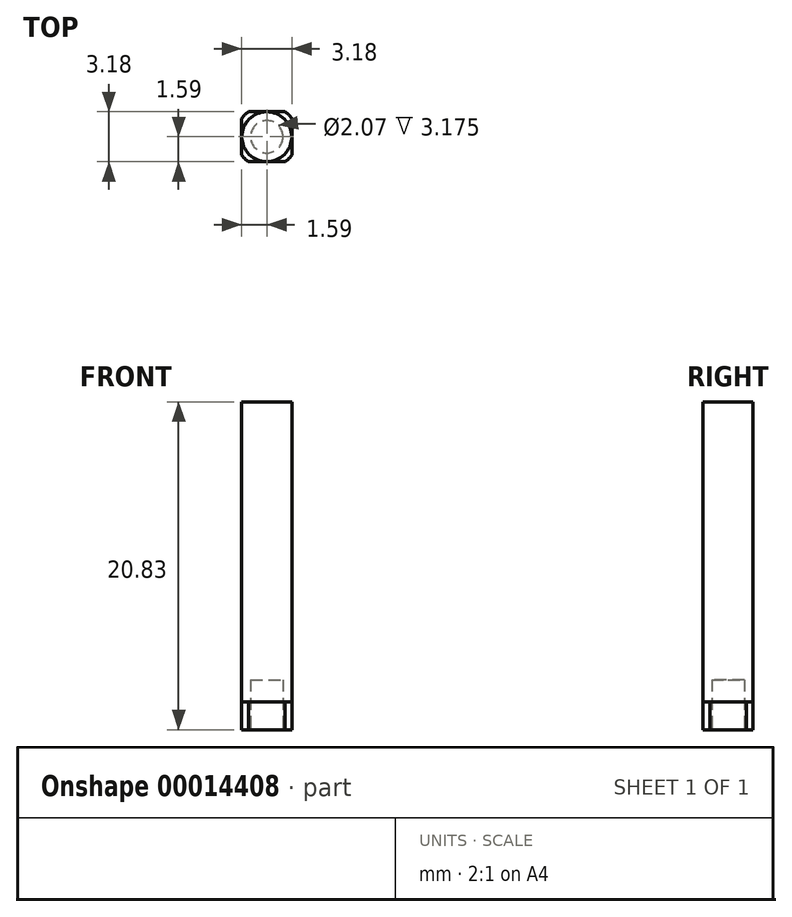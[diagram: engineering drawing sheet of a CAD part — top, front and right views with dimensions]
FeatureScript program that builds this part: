
annotation { "Feature Type Name" : "Feature", "Feature Type Description" : "" }
export const myFeature = defineFeature(function(context is Context, id is Id, definition is map)
    precondition{}
    {
        {
            var Q0;
            Q0=qCreatedBy(makeId("Top.planeOp"),FACE);
            var sketch = newSketch(context, id + "F0", { "sketchPlane" : qUnion([Q0])});
            skLineSegment(sketch, "E0.rect.bottom", {"start": v(1.16, 1.59) * mm, "end": v(-1.16, 1.59) * mm});
            skLineSegment(sketch, "E0.rect.top", {"start": v(1.16, -1.59) * mm, "end": v(-1.16, -1.59) * mm});
            skLineSegment(sketch, "E0.rect.left", {"start": v(1.59, 1.16) * mm, "end": v(1.59, -1.16) * mm});
            skLineSegment(sketch, "E0.rect.right", {"start": v(-1.59, 1.16) * mm, "end": v(-1.59, -1.16) * mm});
            skPoint(sketch, "E0.rect.middle", {"position": v(0, 0) * mm});
            skArc(sketch, "E1", {"start": v(-1.16, 1.59) * mm, "mid": v(-1.4, 1.4) * mm, "end": v(-1.59, 1.16) * mm});
            skPoint(sketch, "E2.orphan", {"position": v(1.59, 1.59) * mm});
            skPoint(sketch, "E3.orphan", {"position": v(-1.59, 1.59) * mm});
            skArc(sketch, "E4.trimOffspring", {"start": v(-1.59, -1.16) * mm, "mid": v(-1.4, -1.4) * mm, "end": v(-1.16, -1.59) * mm});
            skPoint(sketch, "E5.orphan", {"position": v(-1.59, -1.59) * mm});
            skArc(sketch, "E6.trimOffspring", {"start": v(1.16, -1.59) * mm, "mid": v(1.4, -1.4) * mm, "end": v(1.59, -1.16) * mm});
            skPoint(sketch, "E7.orphan", {"position": v(1.59, -1.59) * mm});
            skArc(sketch, "E8.trimOffspring", {"start": v(1.59, 1.16) * mm, "mid": v(1.4, 1.4) * mm, "end": v(1.16, 1.59) * mm});
            skSolve(sketch);
        }
        {
            var Q0;
            Q0=qSketchRegion(id+"F0",true);
            extrude(context, id + "F1", {"entities" : qUnion([Q0]), "depth" : ((1 + 7 / 8) - 3 / 32) * mm});
        }
        {
            var Q0;
            Q0=makeQuery(id+"F1.opExtrude","CAP_FACE",FACE,{"disambiguationData":[OSD([sQuery(id+"F0.wireOp",EDGE,"E0.rect.bottom"),sQuery(id+"F0.wireOp",EDGE,"E0.rect.top"),sQuery(id+"F0.wireOp",EDGE,"E0.rect.left"),sQuery(id+"F0.wireOp",EDGE,"E0.rect.right"),sQuery(id+"F0.wireOp",EDGE,"E1"),sQuery(id+"F0.wireOp",EDGE,"E4.trimOffspring"),sQuery(id+"F0.wireOp",EDGE,"E6.trimOffspring"),sQuery(id+"F0.wireOp",EDGE,"E8.trimOffspring")])],"isStart":false});
            var sketch = newSketch(context, id + "F2", { "sketchPlane" : qUnion([Q0])});
            skCircle(sketch, "E9", {"center": v(0, 0) * mm, "radius": 1.59 * mm});
            skSolve(sketch);
        }
        {
            var Q0;
            Q0=qSketchRegion(id+"F2",true);
            extrude(context, id + "F3", {"entities" : qUnion([Q0]), "operationType" : NewBodyOperationType.ADD, "depth" : 19.05 * mm});
        }
        {
            var Q0;
            Q0=makeQuery(id+"F1.opExtrude","CAP_FACE",FACE,{"disambiguationData":[OSD([sQuery(id+"F0.wireOp",EDGE,"E0.rect.bottom"),sQuery(id+"F0.wireOp",EDGE,"E0.rect.top"),sQuery(id+"F0.wireOp",EDGE,"E0.rect.left"),sQuery(id+"F0.wireOp",EDGE,"E0.rect.right"),sQuery(id+"F0.wireOp",EDGE,"E1"),sQuery(id+"F0.wireOp",EDGE,"E4.trimOffspring"),sQuery(id+"F0.wireOp",EDGE,"E6.trimOffspring"),sQuery(id+"F0.wireOp",EDGE,"E8.trimOffspring")])],"isStart":true});
            var sketch = newSketch(context, id + "F4", { "sketchPlane" : qUnion([Q0])});
            skCircle(sketch, "E10", {"center": v(0, 0) * mm, "radius": 1.03 * mm});
            skSolve(sketch);
        }
        {
            var Q0;
            Q0=qSketchRegion(id+"F4",true);
            extrude(context, id + "F5", {"entities" : qUnion([Q0]), "operationType" : NewBodyOperationType.REMOVE, "oppositeDirection" : true, "depth" : 3.17 * mm});
        }
    });
